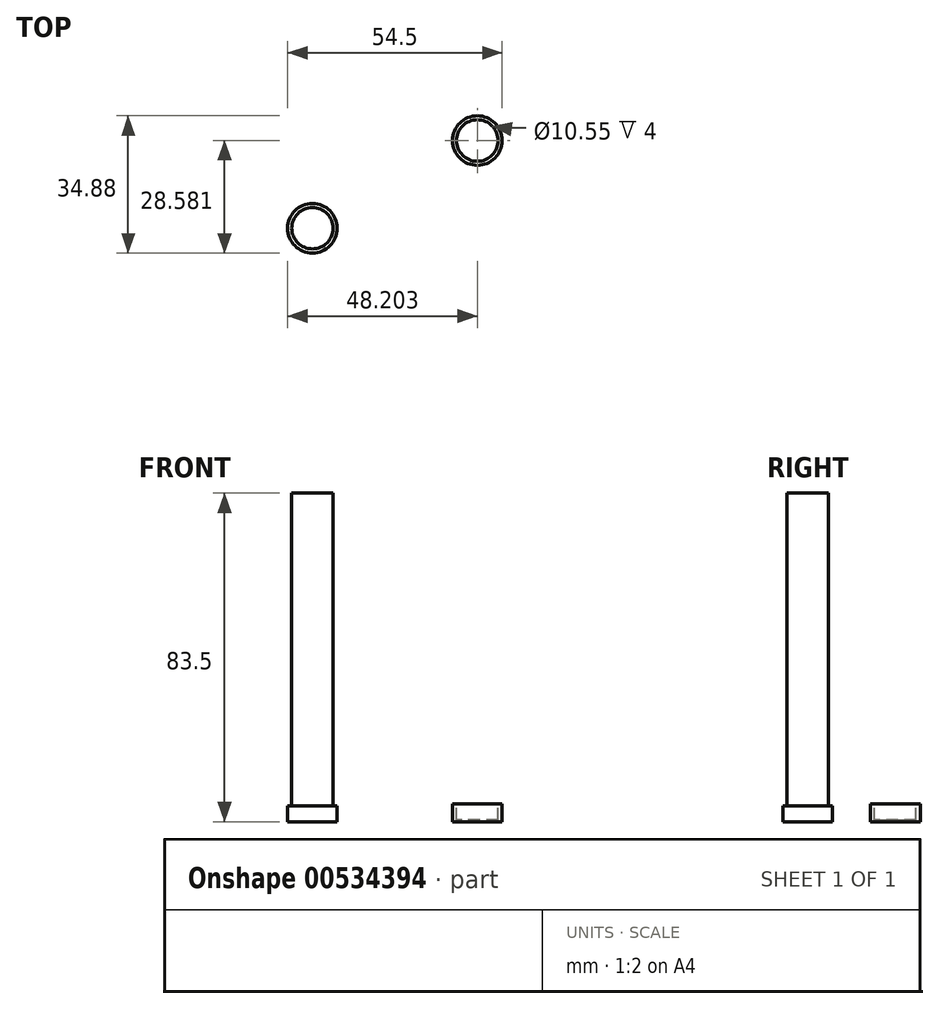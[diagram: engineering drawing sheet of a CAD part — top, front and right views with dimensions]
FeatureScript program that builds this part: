
annotation { "Feature Type Name" : "Feature", "Feature Type Description" : "" }
export const myFeature = defineFeature(function(context is Context, id is Id, definition is map)
    precondition{}
    {
        {
            var Q0;
            Q0=qCreatedBy(makeId("Top.planeOp"),FACE);
            var sketch = newSketch(context, id + "F0", { "sketchPlane" : qUnion([Q0])});
            skCircle(sketch, "E0", {"center": v(0, 0) * mm, "radius": 6.3 * mm});
            skCircle(sketch, "E1", {"center": v(0, 0) * mm, "radius": 5.25 * mm});
            skSolve(sketch);
        }
        {
            var Q0;
            Q0=makeQuery(id+"F0.imprint","IMPRINT",FACE,{"disambiguationData":[TD([[makeQuery(id+"F0.imprint","IMPRINT",EDGE,{"derivedFrom":sQuery(id+"F0.wireOp",EDGE,"E1")}),1.0]])]});
            extrude(context, id + "F1", {"entities" : qUnion([Q0]), "depth" : 84 * mm, "offsetDistance" : 25 * mm});
        }
        {
            var Q0;
            Q0=makeQuery(id+"F0.imprint","IMPRINT",FACE,{"disambiguationData":[TD([[makeQuery(id+"F0.imprint","IMPRINT",EDGE,{"derivedFrom":sQuery(id+"F0.wireOp",EDGE,"E0")}),1.0]])]});
            extrude(context, id + "F2", {"entities" : qUnion([Q0]), "operationType" : NewBodyOperationType.ADD, "depth" : 4 * mm, "offsetDistance" : 25 * mm});
        }
        {
            var Q0;
            Q0=qCreatedBy(makeId("Top.planeOp"),FACE);
            var sketch = newSketch(context, id + "F3", { "sketchPlane" : qUnion([Q0])});
            skCircle(sketch, "E2", {"center": v(41.9, 22.28) * mm, "radius": 6.3 * mm});
            skSolve(sketch);
        }
        {
            var Q0;
            Q0=makeQuery(id+"F3.imprint","IMPRINT",FACE,{"disambiguationData":[TD([[makeQuery(id+"F3.imprint","IMPRINT",EDGE,{"derivedFrom":sQuery(id+"F3.wireOp",EDGE,"E2")}),1.0]])]});
            extrude(context, id + "F4", {"entities" : qUnion([Q0]), "depth" : 4.5 * mm, "offsetDistance" : 25 * mm});
        }
        {
            var Q0;
            Q0=makeQuery(id+"F4.opExtrude","CAP_FACE",FACE,{"disambiguationData":[OSD([sQuery(id+"F3.wireOp",EDGE,"E2")])],"isStart":false});
            var sketch = newSketch(context, id + "F5", { "sketchPlane" : qUnion([Q0])});
            skCircle(sketch, "E3", {"center": v(41.9, 22.28) * mm, "radius": 5.28 * mm});
            skSolve(sketch);
        }
        {
            var Q0;
            Q0=makeQuery(id+"F5.imprint","IMPRINT",FACE,{"disambiguationData":[TD([[makeQuery(id+"F5.imprint","IMPRINT",EDGE,{"derivedFrom":sQuery(id+"F5.wireOp",EDGE,"E3")}),1.0]])]});
            extrude(context, id + "F6", {"entities" : qUnion([Q0]), "operationType" : NewBodyOperationType.REMOVE, "oppositeDirection" : true, "depth" : 4 * mm, "offsetDistance" : 25 * mm});
        }
        {
            var Q0;
            Q0=makeQuery(id+"F1.opExtrude","CAP_FACE",FACE,{"disambiguationData":[OSD([sQuery(id+"F0.wireOp",EDGE,"E1")])],"isStart":false});
            extrude(context, id + "F7", {"entities" : qUnion([Q0]), "operationType" : NewBodyOperationType.REMOVE, "oppositeDirection" : true, "depth" : 0.5 * mm, "offsetDistance" : 25 * mm});
        }
    });
